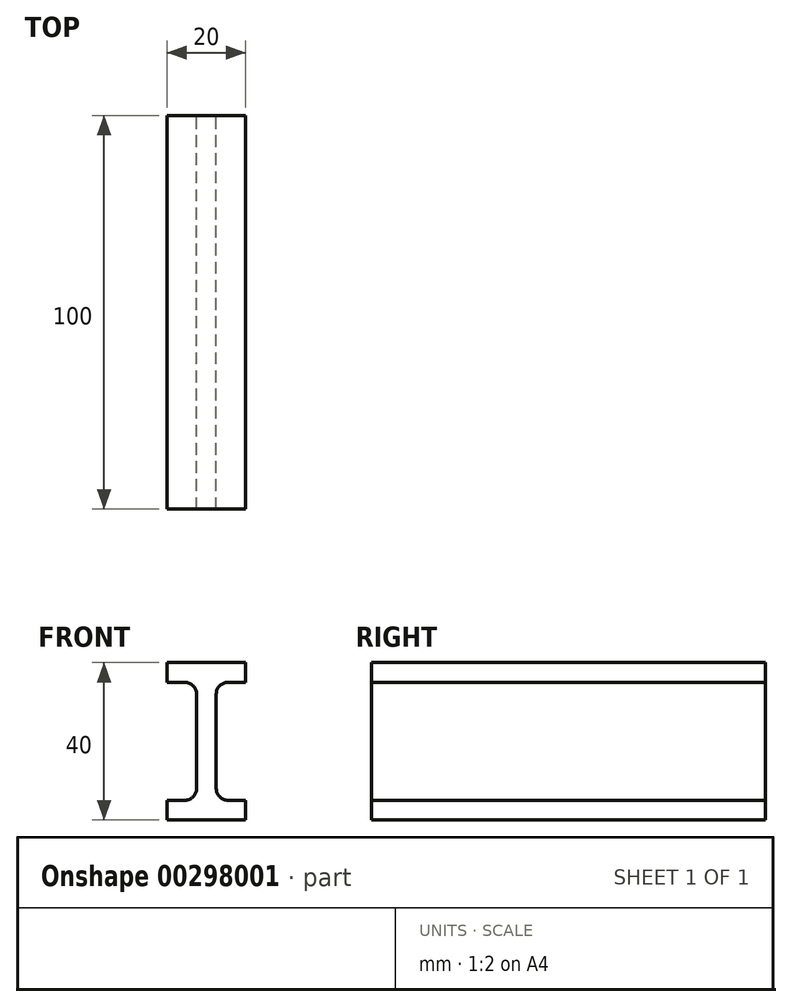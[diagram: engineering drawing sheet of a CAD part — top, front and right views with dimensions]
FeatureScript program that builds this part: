
annotation { "Feature Type Name" : "Feature", "Feature Type Description" : "" }
export const myFeature = defineFeature(function(context is Context, id is Id, definition is map)
    precondition{}
    {
        {
            var Q0;
            Q0=qCreatedBy(makeId("Front.planeOp"),FACE);
            var sketch = newSketch(context, id + "F0", { "sketchPlane" : qUnion([Q0])});
            skLineSegment(sketch, "E0", {"start": v(0, 40) * mm, "end": v(10, 40) * mm});
            skLineSegment(sketch, "E1", {"start": v(10, 40) * mm, "end": v(10, 35) * mm});
            skLineSegment(sketch, "E2", {"start": v(10, 35) * mm, "end": v(5.5, 35) * mm});
            skLineSegment(sketch, "E3", {"start": v(2.5, 32) * mm, "end": v(2.5, 8) * mm});
            skLineSegment(sketch, "E4", {"start": v(5.5, 5) * mm, "end": v(10, 5) * mm});
            skLineSegment(sketch, "E5", {"start": v(10, 5) * mm, "end": v(10, 0) * mm});
            skLineSegment(sketch, "E6", {"start": v(10, 0) * mm, "end": v(0, 0) * mm});
            skPoint(sketch, "E7.visualSharp", {"position": v(2.5, 35) * mm});
            skArc(sketch, "E7.filletArc", {"start": v(5.5, 35) * mm, "mid": v(3.38, 34.12) * mm, "end": v(2.5, 32) * mm});
            skPoint(sketch, "E8.visualSharp", {"position": v(2.5, 5) * mm});
            skArc(sketch, "E8.filletArc", {"start": v(2.5, 8) * mm, "mid": v(3.38, 5.88) * mm, "end": v(5.5, 5) * mm});
            skLineSegment(sketch, "E9.MirrorCS", {"start": v(-5.5, 5) * mm, "end": v(-10, 5) * mm});
            skLineSegment(sketch, "E10.MirrorCS", {"start": v(-10, 35) * mm, "end": v(-5.5, 35) * mm});
            skArc(sketch, "E11.MirrorCS", {"start": v(-5.5, 35) * mm, "mid": v(-3.38, 34.12) * mm, "end": v(-2.5, 32) * mm});
            skArc(sketch, "E12.MirrorCS", {"start": v(-2.5, 8) * mm, "mid": v(-3.38, 5.88) * mm, "end": v(-5.5, 5) * mm});
            skPoint(sketch, "E13.MirrorP", {"position": v(-2.5, 35) * mm});
            skLineSegment(sketch, "E14.MirrorCS", {"start": v(-2.5, 32) * mm, "end": v(-2.5, 8) * mm});
            skPoint(sketch, "E15.MirrorP", {"position": v(-2.5, 5) * mm});
            skLineSegment(sketch, "E16.MirrorCS", {"start": v(-10, 0) * mm, "end": v(0, 0) * mm});
            skLineSegment(sketch, "E17.MirrorCS", {"start": v(-10, 40) * mm, "end": v(-10, 35) * mm});
            skLineSegment(sketch, "E18.MirrorCS", {"start": v(0, 40) * mm, "end": v(-10, 40) * mm});
            skLineSegment(sketch, "E19.MirrorCS", {"start": v(-10, 5) * mm, "end": v(-10, 0) * mm});
            skSolve(sketch);
        }
        {
            var Q0;
            Q0=makeQuery(id+"F0.imprint","IMPRINT",FACE,{"disambiguationData":[TD([[makeQuery(id+"F0.imprint","IMPRINT",EDGE,{"derivedFrom":sQuery(id+"F0.wireOp",EDGE,"E0")}),-1.0]])]});
            extrude(context, id + "F1", {"entities" : qUnion([Q0]), "endBound" : BoundingType.SYMMETRIC, "depth" : 100 * mm});
        }
    });
